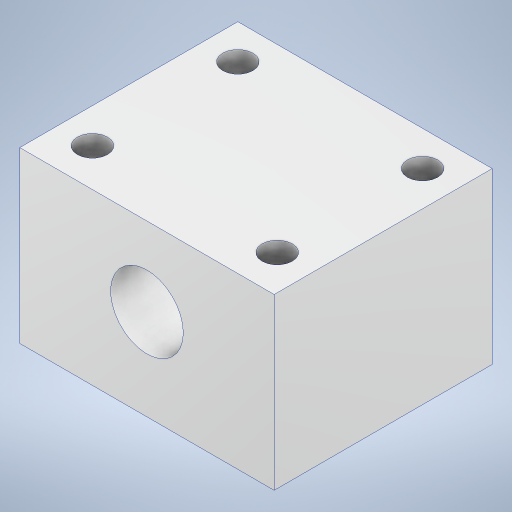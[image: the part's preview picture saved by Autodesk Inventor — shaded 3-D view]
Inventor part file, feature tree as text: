
AUTODESK INVENTOR PART (.ipt)
format: ipt  version: 2023.2 (Build 272271000, 271)  size: 219,648 bytes
history: native  units: mm
features: extrude x2, sketch x2, projected_geometry x1
ambient origin geometry x8: Origin, YZ Plane, XZ Plane, XY Plane, X Axis, Y Axis, Z Axis, Center Point
bodies: Solid1 (feature_tree)
feature tree (5):
  extrude  "Extrusion1"  Depth=28.0mm
  extrude  "Extrusion2"  Depth=36.0mm
  sketch  "Sketch1"  dims[d0=42.0mm d2=28.0mm]
  sketch  "Sketch2"  dims[d3=90.0deg d4=12.0mm d5=15.0mm d6=36.0mm d7=0.0mm d8=5.75mm d9=5.75mm d10=5.0mm d11=12.0mm d12=15.25mm d13=0.0mm d14=0.0mm]
  projected_geometry  "Projected Loop1"
